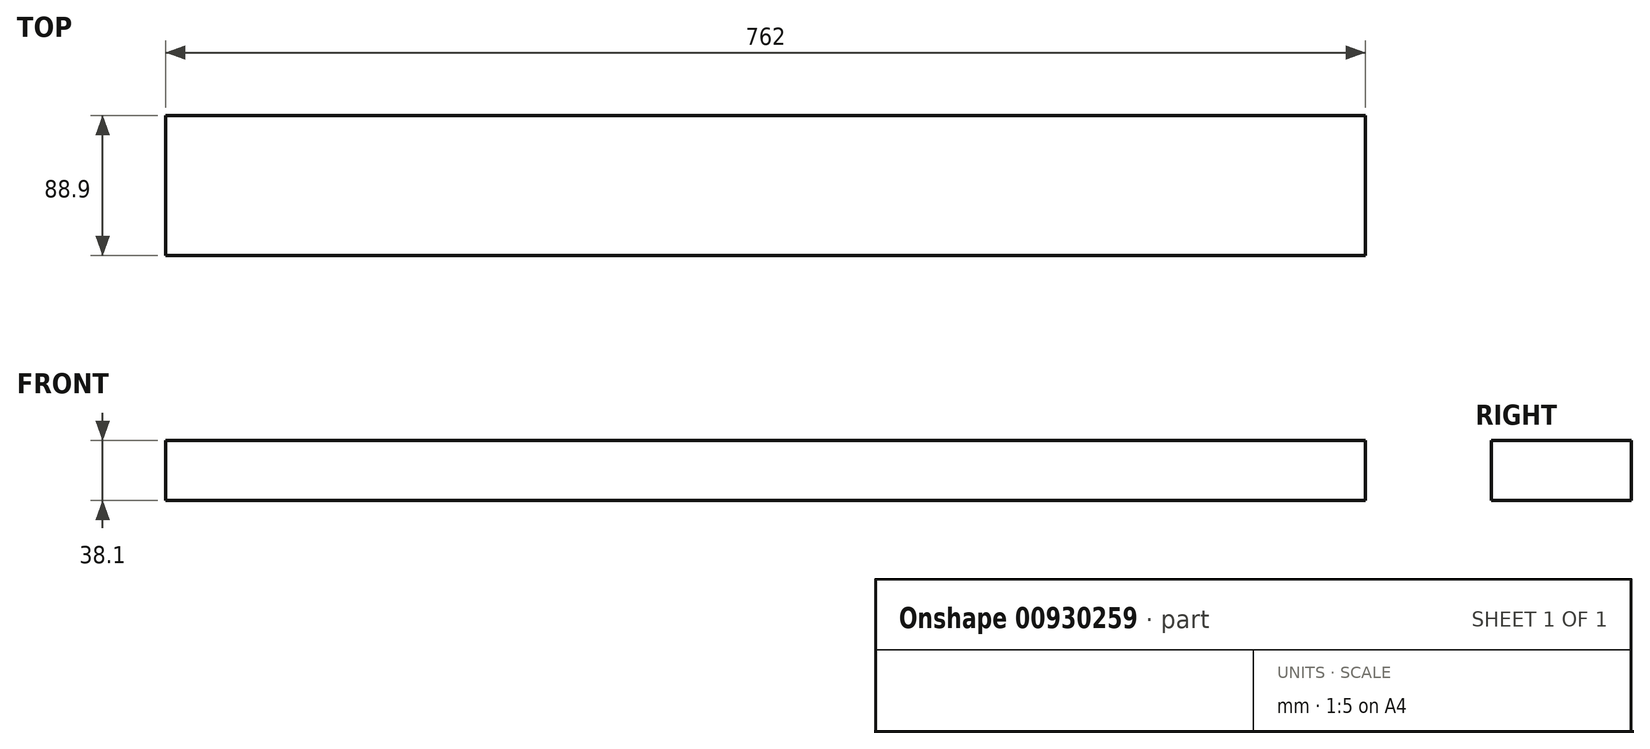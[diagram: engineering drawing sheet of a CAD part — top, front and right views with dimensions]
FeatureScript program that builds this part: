
annotation { "Feature Type Name" : "Feature", "Feature Type Description" : "" }
export const myFeature = defineFeature(function(context is Context, id is Id, definition is map)
    precondition{}
    {
        {
            var Q0;
            Q0=qCreatedBy(makeId("Right.planeOp"),FACE);
            var sketch = newSketch(context, id + "F0", { "sketchPlane" : qUnion([Q0])});
            skLineSegment(sketch, "E0.bottom", {"start": v(44.45, -19.05) * mm, "end": v(-44.45, -19.05) * mm});
            skLineSegment(sketch, "E0.top", {"start": v(44.45, 19.05) * mm, "end": v(-44.45, 19.05) * mm});
            skLineSegment(sketch, "E0.left", {"start": v(44.45, -19.05) * mm, "end": v(44.45, 19.05) * mm});
            skLineSegment(sketch, "E0.right", {"start": v(-44.45, -19.05) * mm, "end": v(-44.45, 19.05) * mm});
            skPoint(sketch, "E0.middle", {"position": v(0, 0) * mm});
            skSolve(sketch);
        }
        {
            var Q0;
            Q0=qSketchRegion(id+"F0",true);
            extrude(context, id + "F1", {"entities" : qUnion([Q0]), "endBound" : BoundingType.SYMMETRIC, "depth" : 762 * mm});
        }
    });
